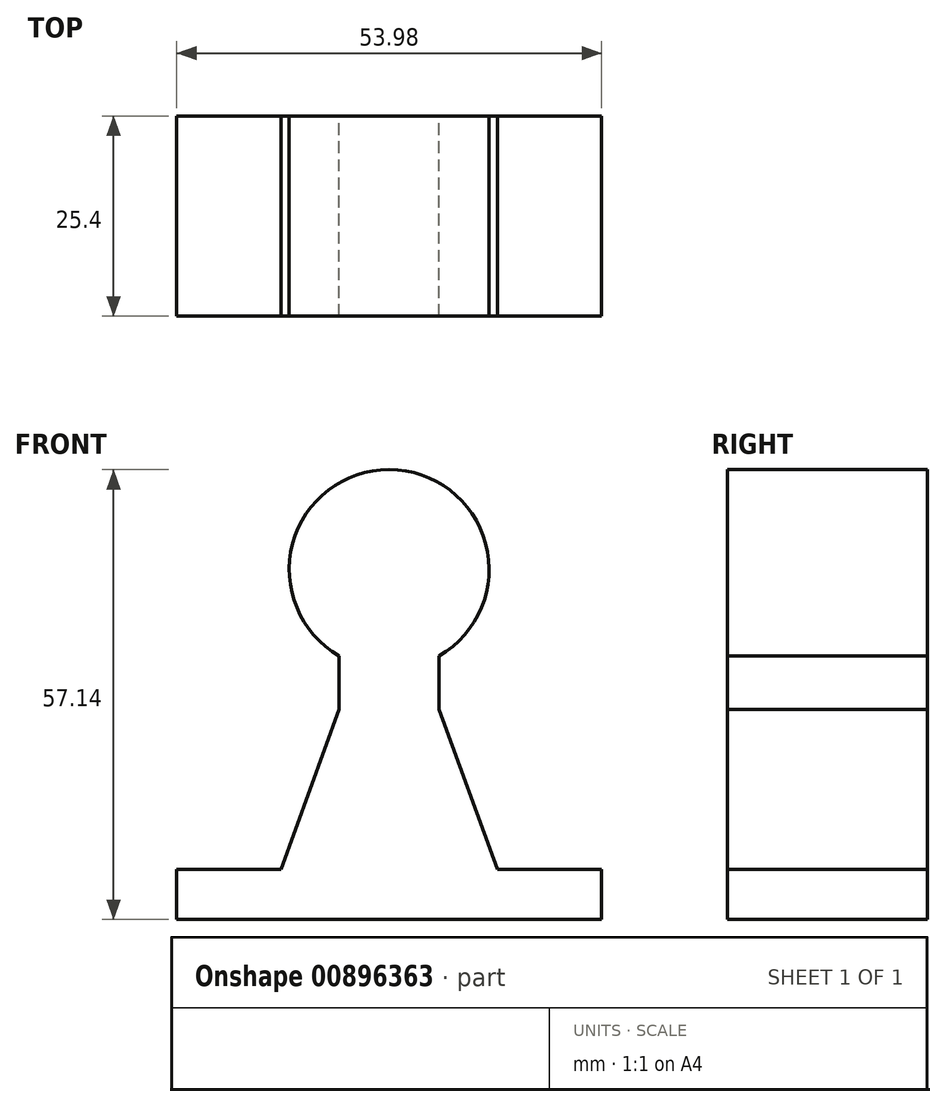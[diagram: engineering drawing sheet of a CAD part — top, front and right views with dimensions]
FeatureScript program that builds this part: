
annotation { "Feature Type Name" : "Feature", "Feature Type Description" : "" }
export const myFeature = defineFeature(function(context is Context, id is Id, definition is map)
    precondition{}
    {
        {
            var Q0;
            Q0=qCreatedBy(makeId("Front.planeOp"),FACE);
            var sketch = newSketch(context, id + "F0", { "sketchPlane" : qUnion([Q0])});
            skArc(sketch, "E0", {"start": v(6.35, -11) * mm, "mid": v(0, 12.7) * mm, "end": v(-6.35, -11) * mm});
            skLineSegment(sketch, "E1.bottom", {"start": v(-26.99, -44.45) * mm, "end": v(26.99, -44.45) * mm});
            skLineSegment(sketch, "E1.top", {"start": v(-26.99, -38.1) * mm, "end": v(-13.75, -38.1) * mm});
            skLineSegment(sketch, "E1.left", {"start": v(-26.99, -44.45) * mm, "end": v(-26.99, -38.1) * mm});
            skLineSegment(sketch, "E1.right", {"start": v(26.99, -44.45) * mm, "end": v(26.99, -38.1) * mm});
            skLineSegment(sketch, "E2", {"start": v(-6.35, -11) * mm, "end": v(-6.35, -17.78) * mm});
            skLineSegment(sketch, "E3", {"start": v(0, 17.65) * mm, "end": v(0, -48.78) * mm, "construction": true});
            skLineSegment(sketch, "E4.MirrorCS", {"start": v(6.35, -11) * mm, "end": v(6.35, -17.78) * mm});
            skLineSegment(sketch, "E5", {"start": v(-6.35, -17.78) * mm, "end": v(-13.75, -38.1) * mm});
            skLineSegment(sketch, "E6.trimOffspring", {"start": v(13.75, -38.1) * mm, "end": v(26.99, -38.1) * mm});
            skLineSegment(sketch, "E7.MirrorCS", {"start": v(6.35, -17.78) * mm, "end": v(13.75, -38.1) * mm});
            skSolve(sketch);
        }
        {
            var Q0;
            Q0=makeQuery(id+"F0.imprint","IMPRINT",FACE,{"disambiguationData":[TD([[makeQuery(id+"F0.imprint","IMPRINT",EDGE,{"derivedFrom":sQuery(id+"F0.wireOp",EDGE,"E0")}),1.0]])]});
            extrude(context, id + "F1", {"entities" : qUnion([Q0]), "depth" : 25.4 * mm, "offsetDistance" : 25.4 * mm});
        }
    });
